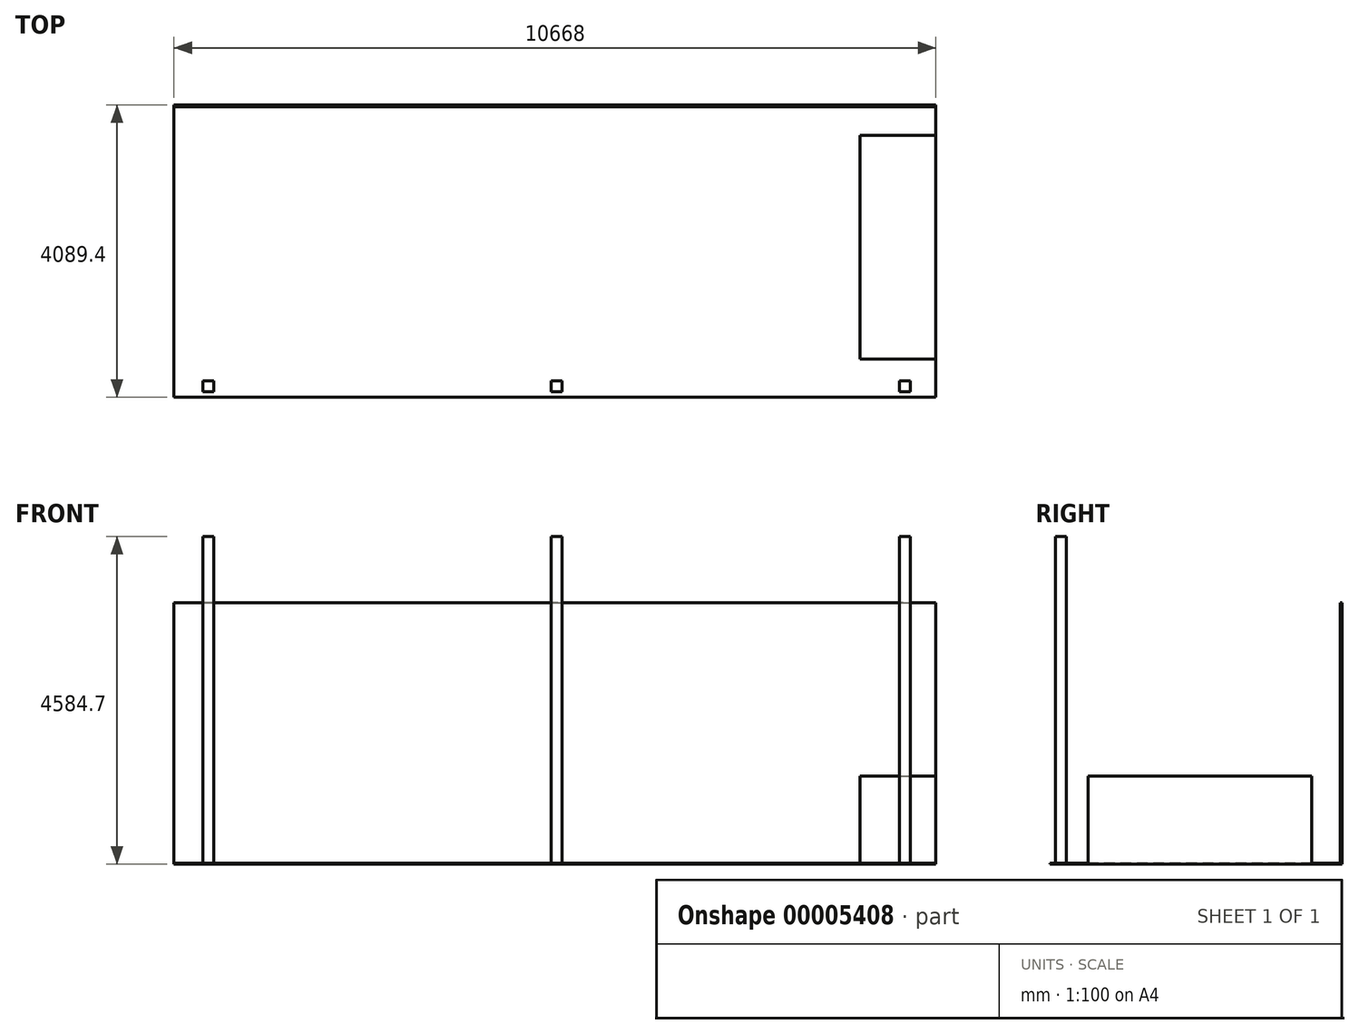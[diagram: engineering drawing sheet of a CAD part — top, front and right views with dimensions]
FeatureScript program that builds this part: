
annotation { "Feature Type Name" : "Feature", "Feature Type Description" : "" }
export const myFeature = defineFeature(function(context is Context, id is Id, definition is map)
    precondition{}
    {
        {
            var Q0;
            Q0=qCreatedBy(makeId("Top.planeOp"),FACE);
            var sketch = newSketch(context, id + "F0", { "sketchPlane" : qUnion([Q0])});
            skLineSegment(sketch, "E0.bottom", {"start": v(0, 0) * mm, "end": v(10668, 0) * mm});
            skLineSegment(sketch, "E0.top", {"start": v(0, 4064) * mm, "end": v(10668, 4064) * mm});
            skLineSegment(sketch, "E0.left", {"start": v(0, 0) * mm, "end": v(0, 4064) * mm});
            skLineSegment(sketch, "E0.right", {"start": v(10668, 0) * mm, "end": v(10668, 4064) * mm});
            skSolve(sketch);
        }
        {
            var Q0;
            Q0 = qSketchRegion(id + "F0", true);
            var Q1;
            Q1 = qBodyType(qCreatedBy(id + "F0" ,EDGE), BodyType.WIRE);
            extrude(context, id + "F1", {"entities" : qUnion([Q0]), "surfaceEntities" : qUnion([Q1]), "depth" : 12.7 * mm});
        }
        {
            var Q0;
            Q0=makeQuery(id+"F1.opExtrude","CAP_FACE",FACE,{"disambiguationData":[OSD([sQuery(id+"F0.wireOp",EDGE,"E0.bottom"),sQuery(id+"F0.wireOp",EDGE,"E0.top"),sQuery(id+"F0.wireOp",EDGE,"E0.left"),sQuery(id+"F0.wireOp",EDGE,"E0.right")])],"isStart":false});
            var sketch = newSketch(context, id + "F2", { "sketchPlane" : qUnion([Q0])});
            skLineSegment(sketch, "E1.bottom", {"start": v(406.4, 228.6) * mm, "end": v(558.8, 228.6) * mm});
            skLineSegment(sketch, "E1.top", {"start": v(406.4, 76.2) * mm, "end": v(558.8, 76.2) * mm});
            skLineSegment(sketch, "E1.left", {"start": v(406.4, 228.6) * mm, "end": v(406.4, 76.2) * mm});
            skLineSegment(sketch, "E1.right", {"start": v(558.8, 228.6) * mm, "end": v(558.8, 76.2) * mm});
            skLineSegment(sketch, "E2.bottom", {"start": v(5283.2, 228.6) * mm, "end": v(5435.6, 228.6) * mm});
            skLineSegment(sketch, "E2.top", {"start": v(5283.2, 76.2) * mm, "end": v(5435.6, 76.2) * mm});
            skLineSegment(sketch, "E2.left", {"start": v(5283.2, 228.6) * mm, "end": v(5283.2, 76.2) * mm});
            skLineSegment(sketch, "E2.right", {"start": v(5435.6, 228.6) * mm, "end": v(5435.6, 76.2) * mm});
            skLineSegment(sketch, "E3.bottom", {"start": v(10160, 228.6) * mm, "end": v(10312.4, 228.6) * mm});
            skLineSegment(sketch, "E3.top", {"start": v(10160, 76.2) * mm, "end": v(10312.4, 76.2) * mm});
            skLineSegment(sketch, "E3.left", {"start": v(10160, 228.6) * mm, "end": v(10160, 76.2) * mm});
            skLineSegment(sketch, "E3.right", {"start": v(10312.4, 228.6) * mm, "end": v(10312.4, 76.2) * mm});
            skSolve(sketch);
        }
        {
            var Q0;
            Q0 = qSketchRegion(id + "F2", true);
            extrude(context, id + "F3", {"entities" : qUnion([Q0]), "operationType" : NewBodyOperationType.ADD, "depth" : 4572 * mm});
        }
        {
            var Q0;
            Q0=makeQuery(id+"F1.opExtrude","CAP_FACE",FACE,{"disambiguationData":[OSD([sQuery(id+"F0.wireOp",EDGE,"E0.bottom"),sQuery(id+"F0.wireOp",EDGE,"E0.top"),sQuery(id+"F0.wireOp",EDGE,"E0.left"),sQuery(id+"F0.wireOp",EDGE,"E0.right")])],"isStart":true});
            var sketch = newSketch(context, id + "F4", { "sketchPlane" : qUnion([Q0])});
            skLineSegment(sketch, "E4.bottom", {"start": v(10668, -4064) * mm, "end": v(0, -4064) * mm});
            skLineSegment(sketch, "E4.top", {"start": v(10668, -4089.4) * mm, "end": v(0, -4089.4) * mm});
            skLineSegment(sketch, "E4.left", {"start": v(10668, -4064) * mm, "end": v(10668, -4089.4) * mm});
            skLineSegment(sketch, "E4.right", {"start": v(0, -4064) * mm, "end": v(0, -4089.4) * mm});
            skSolve(sketch);
        }
        {
            var Q0;
            Q0 = qSketchRegion(id + "F4", true);
            extrude(context, id + "F5", {"entities" : qUnion([Q0]), "oppositeDirection" : true, "depth" : 3657.6 * mm});
        }
        {
            var Q0;
            Q0=makeQuery(id+"F1.opExtrude","CAP_FACE",FACE,{"disambiguationData":[OSD([sQuery(id+"F0.wireOp",EDGE,"E0.bottom"),sQuery(id+"F0.wireOp",EDGE,"E0.top"),sQuery(id+"F0.wireOp",EDGE,"E0.left"),sQuery(id+"F0.wireOp",EDGE,"E0.right")])],"isStart":false});
            var sketch = newSketch(context, id + "F6", { "sketchPlane" : qUnion([Q0])});
            skLineSegment(sketch, "E5.bottom", {"start": v(9606.53, 3664.3) * mm, "end": v(10668, 3664.3) * mm});
            skLineSegment(sketch, "E5.top", {"start": v(9606.53, 533.83) * mm, "end": v(10668, 533.83) * mm});
            skLineSegment(sketch, "E5.left", {"start": v(9606.53, 3664.3) * mm, "end": v(9606.53, 533.83) * mm});
            skLineSegment(sketch, "E5.right", {"start": v(10668, 3664.3) * mm, "end": v(10668, 533.83) * mm});
            skSolve(sketch);
        }
        {
            var Q0;
            Q0 = qSketchRegion(id + "F6", true);
            extrude(context, id + "F7", {"entities" : qUnion([Q0]), "operationType" : NewBodyOperationType.ADD, "depth" : 1219.2 * mm});
        }
    });
